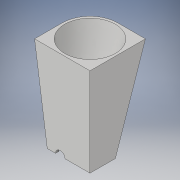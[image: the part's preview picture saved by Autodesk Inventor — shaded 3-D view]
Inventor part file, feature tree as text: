
AUTODESK INVENTOR PART (.ipt)
format: ipt  version: 2018 (Build 220112000, 112)  size: 168,960 bytes
history: native  units: in
note: dims shown in document units (in); Inventor stores cm internally (conversion verified against a paired STEP export)
features: sketch x5, loft x2, plane x1, extrude x1
ambient origin geometry x8: Origin, YZ Plane, XZ Plane, XY Plane, X Axis, Y Axis, Z Axis, Center Point
bodies: Solid1 (feature_tree)
feature tree (9):
  sketch  "Sketch1"  dims[d1=0.8in d2=1.35in]
  plane  "Work Plane1"
  loft  "Loft1"
  loft  "Loft2"
  extrude  "Extrusion1"  Depth=0.875in
  sketch  "Sketch3"  dims[d4=0.4in d5=2.8in]
  sketch  "Sketch4"  dims[d15=0.875in d17=0.875in]
  sketch  "Sketch5"  dims[d18=0.875in]
  sketch  "Sketch6"  dims[d19=0.0in d20=90.0deg d21=0.0in d22=90.0deg d23=1.6in d24=0.875in d26=0.875in d27=0.65in d28=0.0in d29=90.0deg d30=0.0in d31=90.0deg d32=0.4in d33=0.4in d34=0.4in d35=0.15in d36=0.0in d37=0.0in d38=3.0in d39=0.0in]
